# Revit family: IS_ConnectBlue_B0381_BIM_DE
name_source: partatom
category: Plumbing Fixtures
revit_build: Autodesk Revit 2015 (Build: 20140606_1530(x64)
units: mm (PartAtom-declared; Revit-internal decimal feet)

## types (1)
- B0381AA - CONNECT BLUE SNK MXR R-MTD CAST SPT
    Accessories = www.idealspec.co.uk
    AreaUnits = millimeters
    Assembly Code = C1030200
    AssetType = Fixed
    BIMObjectName = ISI_IdealStandard_KitchenSinks_ConnectBlue_B0381
    BarCode = 3800861037576
    Brand = Ideal Standard
    Color = Chromium Plated
    ConnectionType = Plumbing
    Cost = 0 $
    Description = CONNECT BLUE SNK MXR R-MTD CAST SPT
    DurationUnit = year
    Features = CONNECT BLUE SNK MXR R-MTD CAST SPT
    Finish = Chromium Plated
    Help = www.idealstandard.de
    IfcExportAs = IfcValveType
    IfcExportType = KITCHEN MIXERS
    InstallationInstructions = www.idealstandard.de
    LinearUnits = millimeters
    MainColor = Chromium Plated
    MaintenanceInformation = www.idealstandard.de
    Manufacturer = www.idealstandard.de
    ManufacturerURL = www.idealstandard.de
    Model = B0381AA
    ModelNumber = B0381AA
    ModelReference = CONNECT BLUE SNK MXR R-MTD CAST SPT
    Name = KitchenSinks_ConnectBlue_B0381_ISI
    NettWeight = 1,97 KG
    NominalDepth = 272 mm
    NominalHeight = 283 mm
    NominalLength = 272 mm
    NominalWidth = 73 mm
    ProductInformation = www.idealstandard.de
    Shape = Sculptured
    Size = 283 x 272 x 73 mm
    Space = Internal
    SpareParts = www.idealstandard.de
    TestPressure = 10 bar
    URL = www.idealstandard.de
    Uniclass2015Code = Pr_40_20_96_45
    Uniclass2015Title = Kitchen sinks
    Uniclass2015Version = Products v1.1

## geometry (parser evidence)
native form markers: Blend x4
no freeform markers — native parametric forms only
